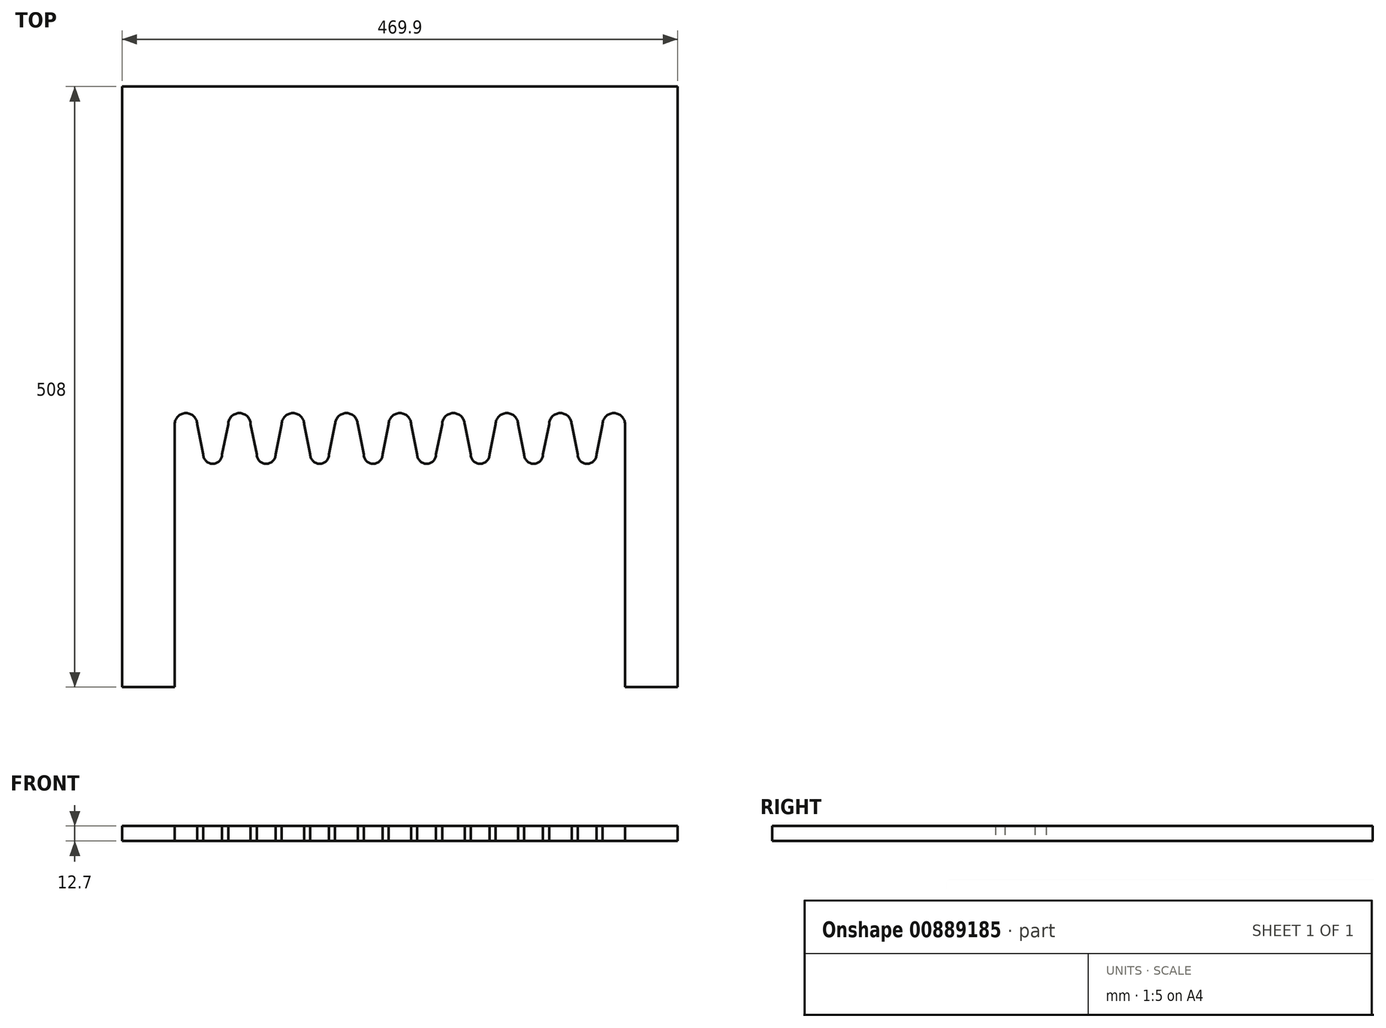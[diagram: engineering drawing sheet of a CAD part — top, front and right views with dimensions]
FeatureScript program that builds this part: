
annotation { "Feature Type Name" : "Feature", "Feature Type Description" : "" }
export const myFeature = defineFeature(function(context is Context, id is Id, definition is map)
    precondition{}
    {
        {
            var Q0;
            Q0=qCreatedBy(makeId("Top.planeOp"),FACE);
            var sketch = newSketch(context, id + "F0", { "sketchPlane" : qUnion([Q0])});
            skLineSegment(sketch, "E0.bottom", {"start": v(-227.8, -254) * mm, "end": v(242.1, -254) * mm});
            skLineSegment(sketch, "E0.top", {"start": v(-227.8, 254) * mm, "end": v(242.1, 254) * mm});
            skLineSegment(sketch, "E0.left", {"start": v(-227.8, -254) * mm, "end": v(-227.8, 254) * mm});
            skLineSegment(sketch, "E0.right", {"start": v(242.1, -254) * mm, "end": v(242.1, 254) * mm});
            skLineSegment(sketch, "E1", {"start": v(197.64, -31.75) * mm, "end": v(197.64, -254) * mm});
            skLineSegment(sketch, "E2.MirrorCS", {"start": v(-183.36, -31.75) * mm, "end": v(-183.36, -254) * mm});
            skLineSegment(sketch, "E3", {"start": v(-227.8, -31.75) * mm, "end": v(242.1, -31.75) * mm});
            skLineSegment(sketch, "E4", {"start": v(7.14, 254) * mm, "end": v(7.14, -31.75) * mm});
            skLineSegment(sketch, "E5", {"start": v(7.14, -31.75) * mm, "end": v(7.14, -50.8) * mm});
            skCircle(sketch, "E6", {"center": v(7.14, -50.8) * mm, "radius": 7.94 * mm});
            skCircle(sketch, "E7", {"center": v(188.12, -31.75) * mm, "radius": 9.53 * mm});
            skCircle(sketch, "E8", {"center": v(142.88, -31.75) * mm, "radius": 9.53 * mm});
            skLineSegment(sketch, "E9", {"start": v(142.88, -31.75) * mm, "end": v(188.12, -31.75) * mm});
            skLineSegment(sketch, "E10", {"start": v(165.5, -31.75) * mm, "end": v(165.5, -57.15) * mm});
            skCircle(sketch, "E11", {"center": v(165.5, -57.15) * mm, "radius": 7.94 * mm});
            skLineSegment(sketch, "E12", {"start": v(152.4, -31.75) * mm, "end": v(157.56, -57.15) * mm});
            skLineSegment(sketch, "E13", {"start": v(178.6, -31.75) * mm, "end": v(173.43, -57.15) * mm});
            skLineSegment(sketch, "E14.1.0.1", {"start": v(133.35, -31.75) * mm, "end": v(128.2, -57.15) * mm});
            skCircle(sketch, "E14.1.0.2", {"center": v(120.25, -57.15) * mm, "radius": 7.94 * mm});
            skLineSegment(sketch, "E14.1.0.3", {"start": v(107.16, -31.75) * mm, "end": v(112.32, -57.15) * mm});
            skCircle(sketch, "E14.2.0.0", {"center": v(97.63, -31.75) * mm, "radius": 9.53 * mm});
            skLineSegment(sketch, "E14.2.0.1", {"start": v(88.1, -31.75) * mm, "end": v(82.95, -57.15) * mm});
            skCircle(sketch, "E14.2.0.2", {"center": v(75, -57.15) * mm, "radius": 7.94 * mm});
            skLineSegment(sketch, "E14.2.0.3", {"start": v(61.91, -31.75) * mm, "end": v(67.07, -57.15) * mm});
            skCircle(sketch, "E14.3.0.0", {"center": v(52.39, -31.75) * mm, "radius": 9.53 * mm});
            skLineSegment(sketch, "E14.3.0.1", {"start": v(42.86, -31.75) * mm, "end": v(37.7, -57.15) * mm});
            skCircle(sketch, "E14.3.0.2", {"center": v(29.77, -57.15) * mm, "radius": 7.94 * mm});
            skLineSegment(sketch, "E14.3.0.3", {"start": v(16.67, -31.75) * mm, "end": v(21.83, -57.15) * mm});
            skCircle(sketch, "E14.4.0.0", {"center": v(7.14, -31.75) * mm, "radius": 9.53 * mm});
            skLineSegment(sketch, "E14.4.0.1", {"start": v(-2.38, -31.75) * mm, "end": v(-7.54, -57.15) * mm});
            skCircle(sketch, "E14.4.0.2", {"center": v(-15.48, -57.15) * mm, "radius": 7.94 * mm});
            skLineSegment(sketch, "E14.4.0.3", {"start": v(-28.57, -31.75) * mm, "end": v(-23.42, -57.15) * mm});
            skCircle(sketch, "E14.5.0.0", {"center": v(-38.1, -31.75) * mm, "radius": 9.53 * mm});
            skLineSegment(sketch, "E14.5.0.1", {"start": v(-47.62, -31.75) * mm, "end": v(-52.78, -57.15) * mm});
            skCircle(sketch, "E14.5.0.2", {"center": v(-60.72, -57.15) * mm, "radius": 7.94 * mm});
            skLineSegment(sketch, "E14.5.0.3", {"start": v(-73.82, -31.75) * mm, "end": v(-68.66, -57.15) * mm});
            skCircle(sketch, "E14.6.0.0", {"center": v(-83.34, -31.75) * mm, "radius": 9.53 * mm});
            skLineSegment(sketch, "E14.6.0.1", {"start": v(-92.87, -31.75) * mm, "end": v(-98.03, -57.15) * mm});
            skCircle(sketch, "E14.6.0.2", {"center": v(-105.97, -57.15) * mm, "radius": 7.94 * mm});
            skLineSegment(sketch, "E14.6.0.3", {"start": v(-119.06, -31.75) * mm, "end": v(-113.9, -57.15) * mm});
            skCircle(sketch, "E14.7.0.0", {"center": v(-128.59, -31.75) * mm, "radius": 9.53 * mm});
            skLineSegment(sketch, "E14.7.0.1", {"start": v(-138.11, -31.75) * mm, "end": v(-143.27, -57.15) * mm});
            skCircle(sketch, "E14.7.0.2", {"center": v(-151.2, -57.15) * mm, "radius": 7.94 * mm});
            skLineSegment(sketch, "E14.7.0.3", {"start": v(-164.3, -31.75) * mm, "end": v(-159.15, -57.15) * mm});
            skCircle(sketch, "E14.8.0.0", {"center": v(-173.83, -31.75) * mm, "radius": 9.53 * mm});
            skLineSegment(sketch, "E14.direction1", {"start": v(188.12, -31.75) * mm, "end": v(142.88, -31.75) * mm, "construction": true});
            skSolve(sketch);
        }
        {
            var Q0;
            {var subQ7=sQuery(id+"F0.wireOp",EDGE,"E0.top");var subQ14=sQuery(id+"F0.wireOp",EDGE,"E0.left");var subQ15=makeQuery(id+"F0.imprint","INTERSECT",VERTEX,{"derivedFrom":[subQ7,subQ14]});Q0=makeQuery(id+"F0.imprint","IMPRINT",FACE,{"disambiguationData":[TD([[makeQuery(id+"F0.imprint","IMPRINT",EDGE,{"disambiguationData":[TD([[subQ15,-1.0]])],"derivedFrom":subQ7}),-1.0]])]});}
            var Q1;
            {var subQ3=sQuery(id+"F0.wireOp",EDGE,"E2.MirrorCS");Q1=makeQuery(id+"F0.imprint","IMPRINT",FACE,{"disambiguationData":[TD([[makeQuery(id+"F0.imprint","IMPRINT",EDGE,{"derivedFrom":subQ3}),-1.0]])]});}
            var Q2;
            {var subQ3=sQuery(id+"F0.wireOp",EDGE,"E1");Q2=makeQuery(id+"F0.imprint","IMPRINT",FACE,{"disambiguationData":[TD([[makeQuery(id+"F0.imprint","IMPRINT",EDGE,{"derivedFrom":subQ3}),1.0]])]});}
            var Q3;
            {var subQ6=sQuery(id+"F0.wireOp",EDGE,"E0.right");var subQ14=sQuery(id+"F0.wireOp",EDGE,"E0.top");var subQ15=makeQuery(id+"F0.imprint","INTERSECT",VERTEX,{"derivedFrom":[subQ14,subQ6]});Q3=makeQuery(id+"F0.imprint","IMPRINT",FACE,{"disambiguationData":[TD([[makeQuery(id+"F0.imprint","IMPRINT",EDGE,{"disambiguationData":[TD([[subQ15,1.0]])],"derivedFrom":subQ14}),-1.0]])]});}
            var Q4;
            {var subQ3=sQuery(id+"F0.wireOp",EDGE,"E13");Q4=makeQuery(id+"F0.imprint","IMPRINT",FACE,{"disambiguationData":[TD([[makeQuery(id+"F0.imprint","IMPRINT",EDGE,{"derivedFrom":subQ3}),-1.0]])]});}
            var Q5;
            {var subQ3=sQuery(id+"F0.wireOp",EDGE,"E12");Q5=makeQuery(id+"F0.imprint","IMPRINT",FACE,{"disambiguationData":[TD([[makeQuery(id+"F0.imprint","IMPRINT",EDGE,{"derivedFrom":subQ3}),1.0]])]});}
            var Q6;
            {var subQ0=sQuery(id+"F0.wireOp",EDGE,"E11");var subQ1=makeQuery(id+"F0.imprint","INTERSECT",VERTEX,{"derivedFrom":[subQ0,sQuery(id+"F0.wireOp",EDGE,"E13")]});Q6=makeQuery(id+"F0.imprint","IMPRINT",FACE,{"disambiguationData":[TD([[makeQuery(id+"F0.imprint","IMPRINT",EDGE,{"disambiguationData":[TD([[subQ1,-1.0]])],"derivedFrom":subQ0}),1.0]])]});}
            var Q7;
            {var subQ0=sQuery(id+"F0.wireOp",EDGE,"E14.1.0.1");Q7=makeQuery(id+"F0.imprint","IMPRINT",FACE,{"disambiguationData":[TD([[makeQuery(id+"F0.imprint","IMPRINT",EDGE,{"derivedFrom":subQ0}),-1.0]])]});}
            var Q8;
            {var subQ0=sQuery(id+"F0.wireOp",EDGE,"E14.1.0.2");var subQ1=makeQuery(id+"F0.imprint","INTERSECT",VERTEX,{"derivedFrom":[sQuery(id+"F0.wireOp",EDGE,"E14.1.0.1"),subQ0]});Q8=makeQuery(id+"F0.imprint","IMPRINT",FACE,{"disambiguationData":[TD([[makeQuery(id+"F0.imprint","IMPRINT",EDGE,{"disambiguationData":[TD([[subQ1,-1.0]])],"derivedFrom":subQ0}),1.0]])]});}
            var Q9;
            {var subQ0=sQuery(id+"F0.wireOp",EDGE,"E14.2.0.1");Q9=makeQuery(id+"F0.imprint","IMPRINT",FACE,{"disambiguationData":[TD([[makeQuery(id+"F0.imprint","IMPRINT",EDGE,{"derivedFrom":subQ0}),-1.0]])]});}
            var Q10;
            {var subQ0=sQuery(id+"F0.wireOp",EDGE,"E14.2.0.2");var subQ1=makeQuery(id+"F0.imprint","INTERSECT",VERTEX,{"derivedFrom":[sQuery(id+"F0.wireOp",EDGE,"E14.2.0.1"),subQ0]});Q10=makeQuery(id+"F0.imprint","IMPRINT",FACE,{"disambiguationData":[TD([[makeQuery(id+"F0.imprint","IMPRINT",EDGE,{"disambiguationData":[TD([[subQ1,-1.0]])],"derivedFrom":subQ0}),1.0]])]});}
            var Q11;
            {var subQ0=sQuery(id+"F0.wireOp",EDGE,"E14.3.0.1");Q11=makeQuery(id+"F0.imprint","IMPRINT",FACE,{"disambiguationData":[TD([[makeQuery(id+"F0.imprint","IMPRINT",EDGE,{"derivedFrom":subQ0}),-1.0]])]});}
            var Q12;
            {var subQ0=sQuery(id+"F0.wireOp",EDGE,"E14.3.0.2");var subQ1=makeQuery(id+"F0.imprint","INTERSECT",VERTEX,{"derivedFrom":[sQuery(id+"F0.wireOp",EDGE,"E14.3.0.1"),subQ0]});Q12=makeQuery(id+"F0.imprint","IMPRINT",FACE,{"disambiguationData":[TD([[makeQuery(id+"F0.imprint","IMPRINT",EDGE,{"disambiguationData":[TD([[subQ1,-1.0]])],"derivedFrom":subQ0}),1.0]])]});}
            var Q13;
            {var subQ0=sQuery(id+"F0.wireOp",EDGE,"E14.4.0.1");Q13=makeQuery(id+"F0.imprint","IMPRINT",FACE,{"disambiguationData":[TD([[makeQuery(id+"F0.imprint","IMPRINT",EDGE,{"derivedFrom":subQ0}),-1.0]])]});}
            var Q14;
            {var subQ0=sQuery(id+"F0.wireOp",EDGE,"E14.4.0.2");var subQ1=makeQuery(id+"F0.imprint","INTERSECT",VERTEX,{"derivedFrom":[sQuery(id+"F0.wireOp",EDGE,"E14.4.0.1"),subQ0]});Q14=makeQuery(id+"F0.imprint","IMPRINT",FACE,{"disambiguationData":[TD([[makeQuery(id+"F0.imprint","IMPRINT",EDGE,{"disambiguationData":[TD([[subQ1,-1.0]])],"derivedFrom":subQ0}),1.0]])]});}
            var Q15;
            {var subQ0=sQuery(id+"F0.wireOp",EDGE,"E14.5.0.1");Q15=makeQuery(id+"F0.imprint","IMPRINT",FACE,{"disambiguationData":[TD([[makeQuery(id+"F0.imprint","IMPRINT",EDGE,{"derivedFrom":subQ0}),-1.0]])]});}
            var Q16;
            {var subQ0=sQuery(id+"F0.wireOp",EDGE,"E14.5.0.2");var subQ1=makeQuery(id+"F0.imprint","INTERSECT",VERTEX,{"derivedFrom":[sQuery(id+"F0.wireOp",EDGE,"E14.5.0.1"),subQ0]});Q16=makeQuery(id+"F0.imprint","IMPRINT",FACE,{"disambiguationData":[TD([[makeQuery(id+"F0.imprint","IMPRINT",EDGE,{"disambiguationData":[TD([[subQ1,-1.0]])],"derivedFrom":subQ0}),1.0]])]});}
            var Q17;
            {var subQ0=sQuery(id+"F0.wireOp",EDGE,"E14.6.0.1");Q17=makeQuery(id+"F0.imprint","IMPRINT",FACE,{"disambiguationData":[TD([[makeQuery(id+"F0.imprint","IMPRINT",EDGE,{"derivedFrom":subQ0}),-1.0]])]});}
            var Q18;
            {var subQ0=sQuery(id+"F0.wireOp",EDGE,"E14.6.0.2");var subQ1=makeQuery(id+"F0.imprint","INTERSECT",VERTEX,{"derivedFrom":[sQuery(id+"F0.wireOp",EDGE,"E14.6.0.1"),subQ0]});Q18=makeQuery(id+"F0.imprint","IMPRINT",FACE,{"disambiguationData":[TD([[makeQuery(id+"F0.imprint","IMPRINT",EDGE,{"disambiguationData":[TD([[subQ1,-1.0]])],"derivedFrom":subQ0}),1.0]])]});}
            var Q19;
            {var subQ0=sQuery(id+"F0.wireOp",EDGE,"E14.7.0.1");Q19=makeQuery(id+"F0.imprint","IMPRINT",FACE,{"disambiguationData":[TD([[makeQuery(id+"F0.imprint","IMPRINT",EDGE,{"derivedFrom":subQ0}),-1.0]])]});}
            var Q20;
            {var subQ0=sQuery(id+"F0.wireOp",EDGE,"E14.7.0.2");var subQ1=makeQuery(id+"F0.imprint","INTERSECT",VERTEX,{"derivedFrom":[sQuery(id+"F0.wireOp",EDGE,"E14.7.0.1"),subQ0]});Q20=makeQuery(id+"F0.imprint","IMPRINT",FACE,{"disambiguationData":[TD([[makeQuery(id+"F0.imprint","IMPRINT",EDGE,{"disambiguationData":[TD([[subQ1,-1.0]])],"derivedFrom":subQ0}),1.0]])]});}
            extrude(context, id + "F1", {"entities" : qUnion([Q0, Q1, Q2, Q3, Q4, Q5, Q6, Q7, Q8, Q9, Q10, Q11, Q12, Q13, Q14, Q15, Q16, Q17, Q18, Q19, Q20]), "depth" : 12.7 * mm, "offsetDistance" : 25.4 * mm});
        }
    });
